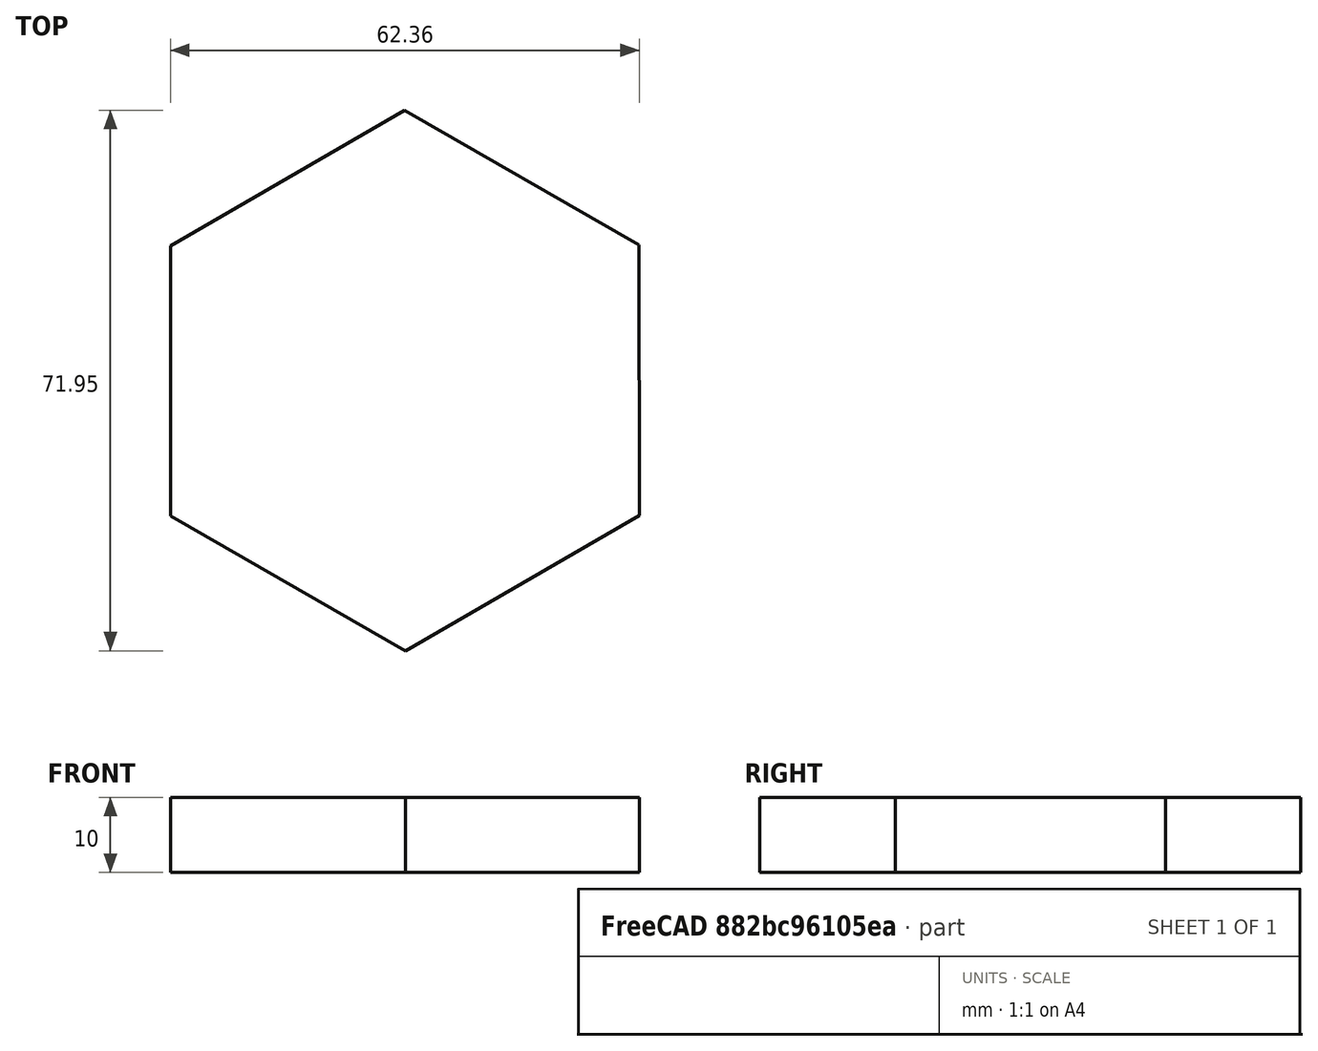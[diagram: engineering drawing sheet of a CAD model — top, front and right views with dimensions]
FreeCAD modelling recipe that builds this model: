
FCSTD DOCUMENT  (FreeCAD 1.0R38642 (Git))
Label: Opgave_1.1.2
License: All rights reserved
LicenseURL: http://en.wikipedia.org/wiki/All_rights_reserved
objects: Sketcher::SketchObject×1, PartDesign::Pad×1, PartDesign::Body×1
note: 6 computed .brp shape members not serialized (recipe doc carries the construction recipe); baked Part::Feature solids carry a one-line shape summary decoded from their .brp

FEATURE [Sketcher::SketchObject] Sketch
  ArcFitTolerance = 1e-06
  AttachmentSupport = -> [XY_Plane]
  FullyConstrained = false
  MakeInternals = false
  MapMode = 5
  sketch-geometry (17):
    g0: LineSegment StartX=96.7236 StartY=31.1383 StartZ=0 EndX=96.6741 EndY=67.1161 EndZ=0
    g1: LineSegment StartX=96.6741 StartY=67.1161 StartZ=0 EndX=65.4917 EndY=85.0621 EndZ=0
    g2: LineSegment StartX=65.4917 StartY=85.0621 StartZ=0 EndX=34.3588 EndY=67.0304 EndZ=0
    g3: LineSegment StartX=34.3588 StartY=67.0304 StartZ=0 EndX=34.4083 EndY=31.0527 EndZ=0
    g4: LineSegment StartX=34.4083 StartY=31.0527 StartZ=0 EndX=65.5907 EndY=13.1066 EndZ=0
    g5: LineSegment StartX=65.5907 StartY=13.1066 StartZ=0 EndX=96.7236 EndY=31.1383 EndZ=0
    g6: Circle [constr] CenterX=65.5412 CenterY=49.0844 CenterZ=0 NormalX=0 NormalY=0 NormalZ=1 AngleXU=0 Radius=35.9778
    g7: Circle CenterX=50.0453 CenterY=61.4527 CenterZ=0 NormalX=0 NormalY=0 NormalZ=1 AngleXU=0 Radius=4.61885
    g8: Circle CenterX=80.0827 CenterY=61.986 CenterZ=0 NormalX=0 NormalY=0 NormalZ=1 AngleXU=0 Radius=5.15796
    g9: ArcOfCircle CenterX=54.3254 CenterY=31.1269 CenterZ=0 NormalX=0 NormalY=0 NormalZ=1 AngleXU=0 Radius=4.05549 StartAngle=1.5708 EndAngle=4.71239
    g10: ArcOfCircle CenterX=77.4117 CenterY=31.1269 CenterZ=0 NormalX=0 NormalY=0 NormalZ=1 AngleXU=0 Radius=4.05549 StartAngle=4.71239 EndAngle=7.85398
    g11: LineSegment StartX=54.3254 StartY=35.1823 StartZ=0 EndX=77.4117 EndY=35.1823 EndZ=0
    g12: LineSegment StartX=54.3254 StartY=27.0714 StartZ=0 EndX=77.4117 EndY=27.0714 EndZ=0
    g13: LineSegment StartX=65.5538 StartY=55.2965 StartZ=0 EndX=60.155 EndY=45.9892 EndZ=0
    g14: LineSegment StartX=60.155 StartY=45.9892 StartZ=0 EndX=70.9148 EndY=45.9674 EndZ=0
    g15: LineSegment StartX=70.9148 StartY=45.9674 StartZ=0 EndX=65.5538 EndY=55.2965 EndZ=0
    g16: Circle [constr] CenterX=65.5412 CenterY=49.0844 CenterZ=0 NormalX=0 NormalY=0 NormalZ=1 AngleXU=0 Radius=6.21217
  constraints (28):
    c: Coincident(g0,g1)
    c: Coincident(g1,g2)
    c: Coincident(g2,g3)
    c: Coincident(g3,g4)
    c: Coincident(g4,g5)
    c: Coincident(g5,g0)
    c: Equal(g0, g1-g5) x5
    c: PointOnObject(g0,g6)
    c: PointOnObject(g1,g6)
    c: PointOnObject(g2,g6)
    c: PointOnObject(g3,g6)
    c: PointOnObject(g4,g6)
    c: PointOnObject(g5,g6)
    c: Tangent(g9,g11) = 1.5708
    c: Tangent(g9,g12) = -1.5708
    c: Tangent(g10,g11) = 1.5708
    c: Tangent(g10,g12) = -1.5708
    c: Equal(g9,g10)
    c: Horizontal(g12)
    c: Coincident(g13,g14)
    c: Coincident(g14,g15)
    c: Coincident(g15,g13)
    c: Equal(g13,g14)
    c: Equal(g13,g15)
    c: PointOnObject(g13,g16)
    c: PointOnObject(g14,g16)
    c: PointOnObject(g15,g16)
    c: Coincident(g6,g16)
FEATURE [PartDesign::Pad] Pad
  Direction = (0,0,1)
  Length = 10
  Length2 = 10
  Profile = -> Sketch [Edge4,Edge3,Edge2,Edge1,Edge6,Edge5]
  ReferenceAxis = -> Sketch [N_Axis]
  Refine = true
  Reversed = true
  Suppressed = false
  Type = 0
FEATURE [PartDesign::Body] Body
  AllowCompound = true
  Group = -> [Sketch,Pad]
  Origin = -> Origin
  Tip = -> Pad
